FCSTD DOCUMENT  (FreeCAD 0.21R33771 (Git))
Label: FilmLooperv3_HandleProfile
License: All rights reserved
objects: Sketcher::SketchObject×1
note: 1 computed .brp shape members not serialized (recipe doc carries the construction recipe); baked Part::Feature solids carry a one-line shape summary decoded from their .brp

FEATURE [Sketcher::SketchObject] Sketch
  FullyConstrained = true
  sketch-geometry (13):
    g0: LineSegment StartX=-15 StartY=82.5 StartZ=0 EndX=15 EndY=82.5 EndZ=0
    g1: LineSegment StartX=15 StartY=82.5 StartZ=0 EndX=15 EndY=-82.5 EndZ=0
    g2: LineSegment StartX=15 StartY=-82.5 StartZ=0 EndX=-15 EndY=-82.5 EndZ=0
    g3: LineSegment StartX=-15 StartY=-82.5 StartZ=0 EndX=-15 EndY=82.5 EndZ=0
    g4: Circle CenterX=0 CenterY=0 CenterZ=0 NormalX=0 NormalY=0 NormalZ=1 AngleXU=0 Radius=3.3
    g5: ArcOfCircle CenterX=0 CenterY=70 CenterZ=0 NormalX=0 NormalY=0 NormalZ=1 AngleXU=0 Radius=3.3 StartAngle=1.5e-15 EndAngle=3.14159
    g6: ArcOfCircle CenterX=0 CenterY=45 CenterZ=0 NormalX=0 NormalY=0 NormalZ=1 AngleXU=0 Radius=3.3 StartAngle=3.14159 EndAngle=6.28319
    g7: LineSegment StartX=-3.3 StartY=70 StartZ=0 EndX=-3.3 EndY=45 EndZ=0
    g8: LineSegment StartX=3.3 StartY=45 StartZ=0 EndX=3.3 EndY=70 EndZ=0
    g9: ArcOfCircle CenterX=0 CenterY=-45 CenterZ=0 NormalX=0 NormalY=0 NormalZ=1 AngleXU=0 Radius=3.3 StartAngle=0 EndAngle=3.14159
    g10: ArcOfCircle CenterX=0 CenterY=-70 CenterZ=0 NormalX=0 NormalY=0 NormalZ=1 AngleXU=0 Radius=3.3 StartAngle=3.14159 EndAngle=6.28319
    g11: LineSegment StartX=-3.3 StartY=-45 StartZ=0 EndX=-3.3 EndY=-70 EndZ=0
    g12: LineSegment StartX=3.3 StartY=-70 StartZ=0 EndX=3.3 EndY=-45 EndZ=0
  constraints (30):
    c: Coincident(g0,g1)
    c: Coincident(g1,g2)
    c: Coincident(g2,g3)
    c: Coincident(g3,g0)
    c: Horizontal(g0)
    c: Horizontal(g2)
    c: Vertical(g1)
    c: Vertical(g3)
    c: Symmetric(g1,g0,g-1)
    c: DistanceX(g0,g0) = 30
    c: DistanceY(g1,g1) = 165
    c: Coincident(g4,g-1)
    c: Radius(g4) = 3.3
    c: Tangent(g5,g7) = -1.5708
    c: Tangent(g7,g6) = -1.5708
    c: Tangent(g6,g8) = -1.5708
    c: Tangent(g8,g5) = -1.5708
    c: Equal(g5,g6)
    c: PointOnObject(g5,g-2)
    c: PointOnObject(g6,g-2)
    c: Tangent(g9,g11) = -1.5708
    c: Tangent(g11,g10) = -1.5708
    c: Tangent(g10,g12) = -1.5708
    c: Tangent(g12,g9) = -1.5708
    c: Symmetric(g10,g5,g4)
    c: Symmetric(g9,g6,g4)
    c: Symmetric(g9,g6,g-1)
    c: Radius(g9) = 3.3
    c: DistanceY(g5) = 70
    c: DistanceY(g6) = 45
